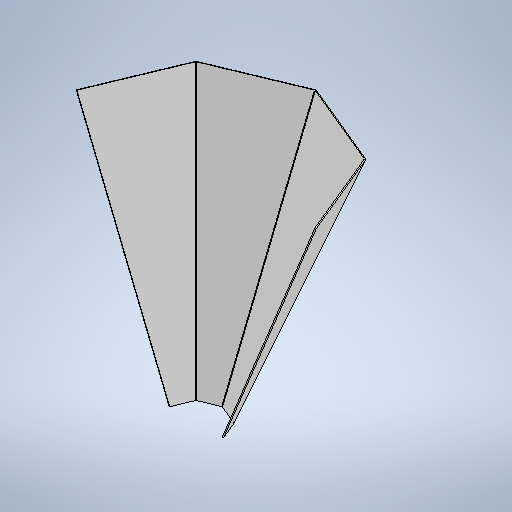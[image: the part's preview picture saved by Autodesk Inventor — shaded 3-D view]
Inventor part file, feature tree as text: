
AUTODESK INVENTOR PART (.ipt)
format: ipt  version: 2025.1 (Build 291241020, 241B)  size: 328,192 bytes
history: native  units: mm
features: sketch x2, plane x1, loft x1, sheet_metal_op x1, other x1
ambient origin geometry x8: Origin, YZ Plane, XZ Plane, XY Plane, X Axis, Y Axis, Z Axis, Center Point
bodies: Body1 (feature_tree)
feature tree (6):
  sketch  "Sketch15"  dims[d116=38.0mm d117=430.0mm]
  plane  "Work Plane1"
  loft  "Lofted Flange1"
  sketch  "Sketch16"  dims[d118=450.0mm d119=2.0mm d120=0.5mm d121=2.0mm d122=2.0mm d123=1.0mm d124=4.0mm d125=2.0mm]
  sheet_metal_op  "Bend1"
  other  "Definition1"
